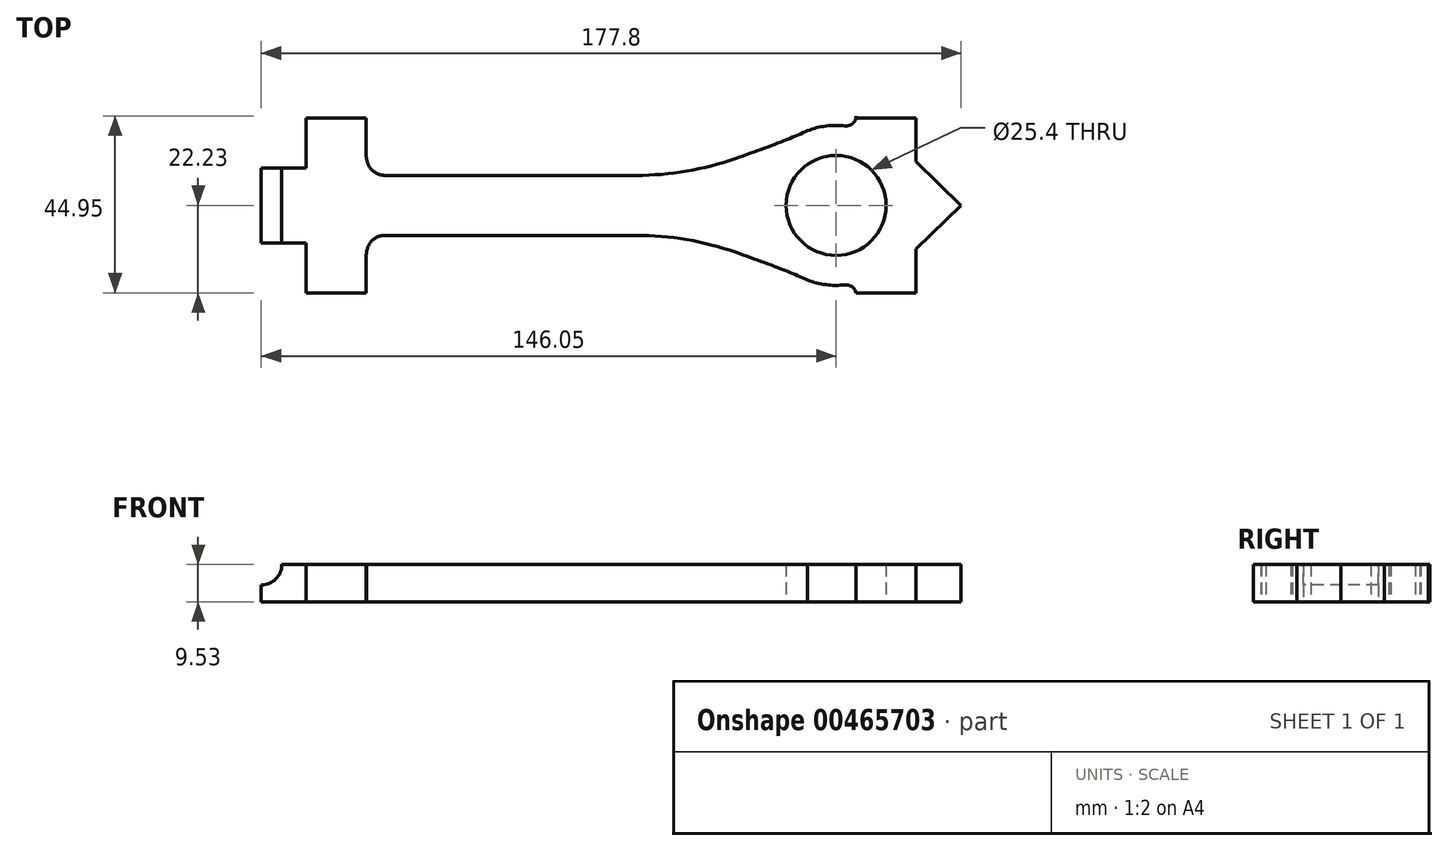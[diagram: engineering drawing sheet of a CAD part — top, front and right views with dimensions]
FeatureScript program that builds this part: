
annotation { "Feature Type Name" : "Feature", "Feature Type Description" : "" }
export const myFeature = defineFeature(function(context is Context, id is Id, definition is map)
    precondition{}
    {
        {
            var Q0;
            Q0=qCreatedBy(makeId("Top.planeOp"),FACE);
            var sketch = newSketch(context, id + "F0", { "sketchPlane" : qUnion([Q0])});
            skPoint(sketch, "E0.endSnap0", {"position": v(69.85, 0) * mm});
            skLineSegment(sketch, "E1.0", {"start": v(7.62, 12.31) * mm, "end": v(7.62, 22.23) * mm});
            skLineSegment(sketch, "E2.0", {"start": v(-7.62, 9.53) * mm, "end": v(-7.62, 22.23) * mm});
            skLineSegment(sketch, "E3.0", {"start": v(147.32, 11.11) * mm, "end": v(147.32, 22.23) * mm});
            skLineSegment(sketch, "E4.0", {"start": v(132.08, 22.23) * mm, "end": v(132.08, 22.72) * mm});
            skLineSegment(sketch, "E5.0", {"start": v(12.37, 7.62) * mm, "end": v(76.22, 7.62) * mm});
            skLineSegment(sketch, "E6.0", {"start": v(-7.62, 9.53) * mm, "end": v(-19.05, 9.52) * mm});
            skLineSegment(sketch, "E7", {"start": v(147.32, 11.11) * mm, "end": v(158.75, 0) * mm});
            skLineSegment(sketch, "E8", {"start": v(132.08, 22.23) * mm, "end": v(147.32, 22.23) * mm});
            skPoint(sketch, "E9.orphan", {"position": v(147.32, 0) * mm});
            skLineSegment(sketch, "E10", {"start": v(-7.62, 22.23) * mm, "end": v(7.62, 22.23) * mm});
            skLineSegment(sketch, "E11", {"start": v(-19.05, 9.52) * mm, "end": v(-19.05, 0) * mm});
            skArc(sketch, "E12", {"start": v(139.7, 0) * mm, "mid": v(127, 12.7) * mm, "end": v(114.3, 0) * mm});
            skArc(sketch, "E13", {"start": v(129.26, 20.2) * mm, "mid": v(124.43, 20.16) * mm, "end": v(119.74, 18.98) * mm});
            skFitSpline(sketch, "E14", {"points": [v(88.96, 7.62) * mm, v(119.74, 18.98) * mm, v(126.88, 23.13) * mm], "startDerivative": vector(54.5, 18.58) * mm, "endDerivative": vector(17.2, 11.68) * mm});
            skArc(sketch, "E15.filletArc", {"start": v(76.22, 7.62) * mm, "mid": v(89, 8.7) * mm, "end": v(101.42, 11.9) * mm});
            skPoint(sketch, "E16.visualSharp", {"position": v(132.08, 19.67) * mm});
            skArc(sketch, "E16.filletArc", {"start": v(129.26, 20.2) * mm, "mid": v(131.23, 20.83) * mm, "end": v(132.08, 22.72) * mm});
            skLineSegment(sketch, "E17.MirrorCS", {"start": v(-19.05, -9.52) * mm, "end": v(-19.05, 0) * mm});
            skLineSegment(sketch, "E18.MirrorCS", {"start": v(-7.62, -9.53) * mm, "end": v(-19.05, -9.52) * mm});
            skLineSegment(sketch, "E19.MirrorCS", {"start": v(-7.62, -9.53) * mm, "end": v(-7.62, -22.23) * mm});
            skLineSegment(sketch, "E20.MirrorCS", {"start": v(-7.62, -22.23) * mm, "end": v(7.62, -22.23) * mm});
            skLineSegment(sketch, "E21.MirrorCS", {"start": v(7.62, -12.31) * mm, "end": v(7.62, -22.23) * mm});
            skLineSegment(sketch, "E22.MirrorCS", {"start": v(12.37, -7.62) * mm, "end": v(76.22, -7.62) * mm});
            skArc(sketch, "E23.MirrorCS", {"start": v(76.22, -7.62) * mm, "mid": v(89, -8.7) * mm, "end": v(101.42, -11.9) * mm});
            skFitSpline(sketch, "E24.MirrorCS", {"points": [v(88.96, -7.62) * mm, v(119.74, -18.98) * mm, v(126.88, -23.13) * mm], "startDerivative": vector(54.5, -18.58) * mm, "endDerivative": vector(17.2, -11.68) * mm});
            skArc(sketch, "E25.MirrorCS", {"start": v(129.26, -20.2) * mm, "mid": v(124.43, -20.16) * mm, "end": v(119.74, -18.98) * mm});
            skArc(sketch, "E26.MirrorCS", {"start": v(129.26, -20.2) * mm, "mid": v(131.04, -20.67) * mm, "end": v(132.03, -22.23) * mm});
            skLineSegment(sketch, "E27.MirrorCS", {"start": v(132.03, -22.23) * mm, "end": v(147.32, -22.23) * mm});
            skLineSegment(sketch, "E28.MirrorCS", {"start": v(147.32, -11.11) * mm, "end": v(147.32, -22.23) * mm});
            skLineSegment(sketch, "E29.MirrorCS", {"start": v(147.32, -11.11) * mm, "end": v(158.75, 0) * mm});
            skArc(sketch, "E30.MirrorCS", {"start": v(139.7, 0) * mm, "mid": v(127, -12.7) * mm, "end": v(114.3, 0) * mm});
            skPoint(sketch, "E31.orphan", {"position": v(132.08, -22.23) * mm});
            skPoint(sketch, "E32.orphan", {"position": v(132.08, -22.72) * mm});
            skPoint(sketch, "E33.start.orphan", {"position": v(0, 0) * mm});
            skArc(sketch, "E34", {"start": v(7.72, 12.31) * mm, "mid": v(9.07, 9) * mm, "end": v(12.37, 7.62) * mm});
            skLineSegment(sketch, "E35", {"start": v(7.62, 12.31) * mm, "end": v(7.72, 12.31) * mm});
            skLineSegment(sketch, "E36", {"start": v(-19.05, 0) * mm, "end": v(0, 0) * mm});
            skArc(sketch, "E37.MirrorCS", {"start": v(7.72, -12.31) * mm, "mid": v(9.07, -9) * mm, "end": v(12.37, -7.62) * mm});
            skLineSegment(sketch, "E38.MirrorCS", {"start": v(7.62, -12.31) * mm, "end": v(7.72, -12.31) * mm});
            skSolve(sketch);
        }
        {
            var Q0;
            Q0 = qSketchRegion(id + "F0", true);
            extrude(context, id + "F1", {"entities" : qUnion([Q0]), "depth" : 9.52 * mm});
        }
        {
            var Q0;
            Q0=makeQuery(id+"F1.opExtrude","SWEPT_FACE",FACE,{"disambiguationData":[OSD([sQuery(id+"F0.wireOp",EDGE,"E18.MirrorCS")])]});
            var sketch = newSketch(context, id + "F2", { "sketchPlane" : qUnion([Q0])});
            skCircle(sketch, "E39", {"center": v(-19.05, 9.53) * mm, "radius": 5.23 * mm});
            skSolve(sketch);
        }
        {
            var Q0;
            Q0 = qSketchRegion(id + "F2", true);
            extrude(context, id + "F3", {"entities" : qUnion([Q0]), "operationType" : NewBodyOperationType.REMOVE, "oppositeDirection" : true, "depth" : 25.4 * mm});
        }
    });
